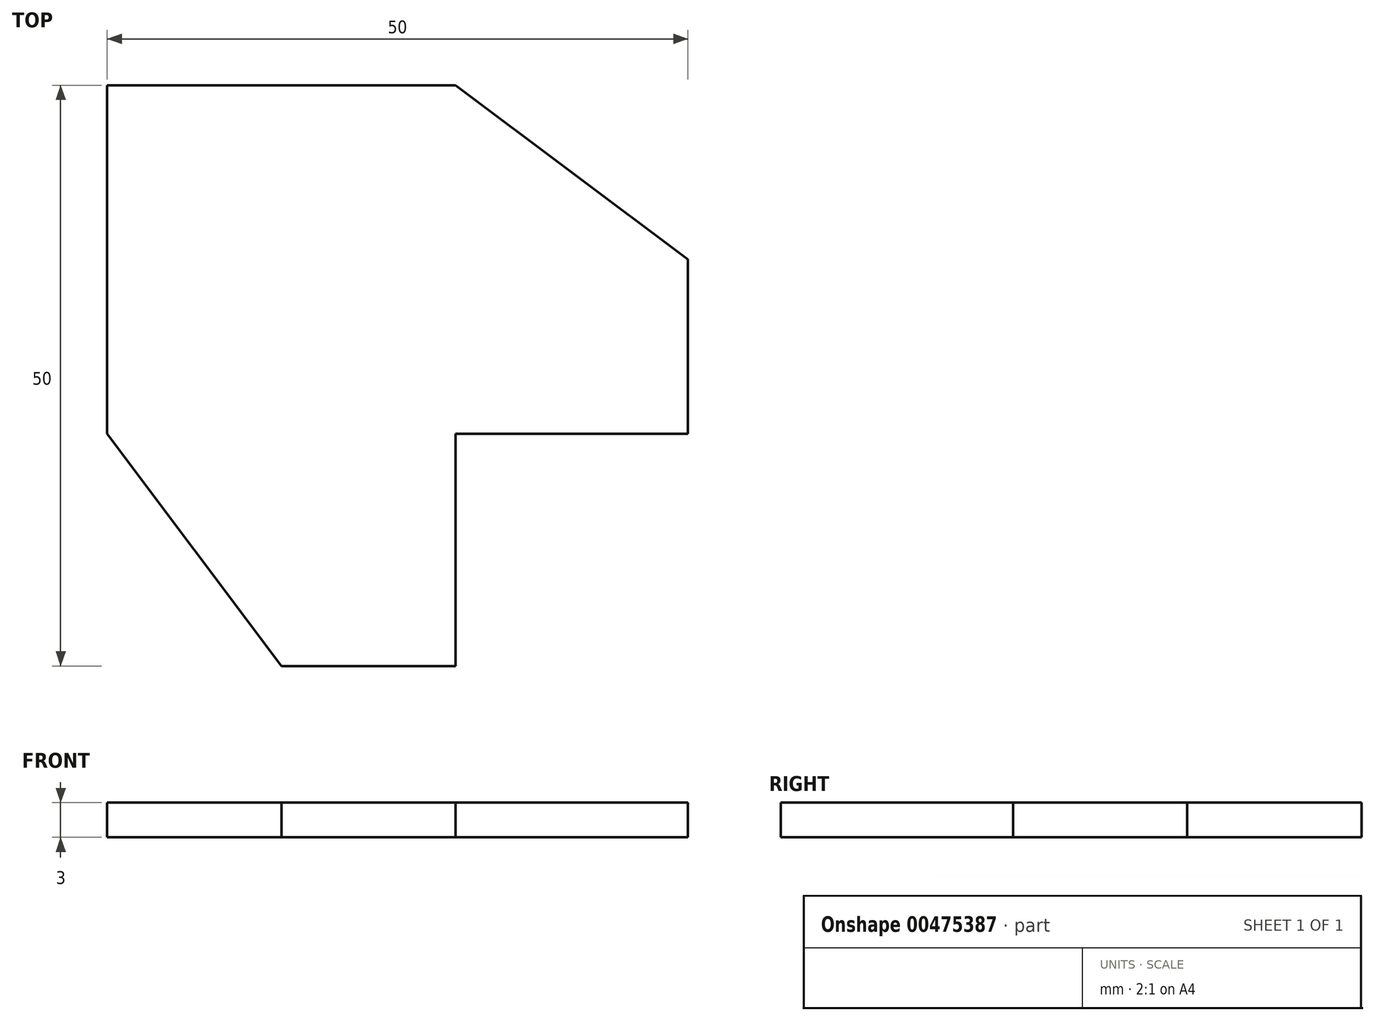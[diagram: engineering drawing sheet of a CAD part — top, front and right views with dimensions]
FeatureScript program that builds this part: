
annotation { "Feature Type Name" : "Feature", "Feature Type Description" : "" }
export const myFeature = defineFeature(function(context is Context, id is Id, definition is map)
    precondition{}
    {
        {
            var Q0;
            Q0=qCreatedBy(makeId("Top.planeOp"),FACE);
            var sketch = newSketch(context, id + "F0", { "sketchPlane" : qUnion([Q0])});
            skLineSegment(sketch, "E0.bottom", {"start": v(0, 0) * mm, "end": v(-15, 0) * mm});
            skLineSegment(sketch, "E0.top", {"start": v(0, -20) * mm, "end": v(-15, -20) * mm});
            skLineSegment(sketch, "E0.left", {"start": v(0, 0) * mm, "end": v(0, -20) * mm});
            skLineSegment(sketch, "E0.right", {"start": v(-15, 0) * mm, "end": v(-15, -20) * mm});
            skLineSegment(sketch, "E1.top", {"start": v(0, 15) * mm, "end": v(-15, 15) * mm});
            skLineSegment(sketch, "E1.left", {"start": v(0, 0) * mm, "end": v(0, 15) * mm});
            skLineSegment(sketch, "E1.right", {"start": v(-15, 0) * mm, "end": v(-15, 15) * mm});
            skLineSegment(sketch, "E2.bottom", {"start": v(0, 0) * mm, "end": v(20, 0) * mm});
            skLineSegment(sketch, "E2.top", {"start": v(0, 15) * mm, "end": v(20, 15) * mm});
            skLineSegment(sketch, "E2.right", {"start": v(20, 0) * mm, "end": v(20, 15) * mm});
            skLineSegment(sketch, "E3.bottom", {"start": v(0, 0) * mm, "end": v(-30, 0) * mm});
            skLineSegment(sketch, "E3.top", {"start": v(0, 30) * mm, "end": v(-30, 30) * mm});
            skLineSegment(sketch, "E3.left", {"start": v(0, 0) * mm, "end": v(0, 30) * mm});
            skLineSegment(sketch, "E3.right", {"start": v(-30, 0) * mm, "end": v(-30, 30) * mm});
            skPoint(sketch, "E3.middle", {"position": v(-15, 15) * mm});
            skLineSegment(sketch, "E4", {"start": v(-30, 0) * mm, "end": v(-15, -20) * mm});
            skLineSegment(sketch, "E5", {"start": v(0, 30) * mm, "end": v(20, 15) * mm});
            skSolve(sketch);
        }
        {
            var Q0;
            {var subQ4=sQuery(id+"F0.wireOp",EDGE,"E1.top");Q0=makeQuery(id+"F0.imprint","IMPRINT",FACE,{"disambiguationData":[TD([[makeQuery(id+"F0.imprint","IMPRINT",EDGE,{"derivedFrom":subQ4}),-1.0]])]});}
            var Q1;
            {var subQ0=sQuery(id+"F0.wireOp",EDGE,"E1.top");Q1=makeQuery(id+"F0.imprint","IMPRINT",FACE,{"disambiguationData":[TD([[makeQuery(id+"F0.imprint","IMPRINT",EDGE,{"derivedFrom":subQ0}),1.0]])]});}
            var Q2;
            {var subQ0=sQuery(id+"F0.wireOp",EDGE,"E2.bottom");Q2=makeQuery(id+"F0.imprint","IMPRINT",FACE,{"disambiguationData":[TD([[makeQuery(id+"F0.imprint","IMPRINT",EDGE,{"derivedFrom":subQ0}),1.0]])]});}
            var Q3;
            Q3=makeQuery(id+"F0.imprint","IMPRINT",FACE,{"disambiguationData":[TD([[makeQuery(id+"F0.imprint","IMPRINT",EDGE,{"derivedFrom":sQuery(id+"F0.wireOp",EDGE,"E0.top")}),-1.0]])]});
            var Q4;
            {var subQ0=sQuery(id+"F0.wireOp",EDGE,"E2.top");Q4=makeQuery(id+"F0.imprint","IMPRINT",FACE,{"disambiguationData":[TD([[makeQuery(id+"F0.imprint","IMPRINT",EDGE,{"derivedFrom":subQ0}),1.0]])]});}
            var Q5;
            {var subQ0=sQuery(id+"F0.wireOp",EDGE,"E0.right");Q5=makeQuery(id+"F0.imprint","IMPRINT",FACE,{"disambiguationData":[TD([[makeQuery(id+"F0.imprint","IMPRINT",EDGE,{"derivedFrom":subQ0}),-1.0]])]});}
            extrude(context, id + "F1", {"entities" : qUnion([Q0, Q1, Q2, Q3, Q4, Q5]), "depth" : 3 * mm});
        }
    });
